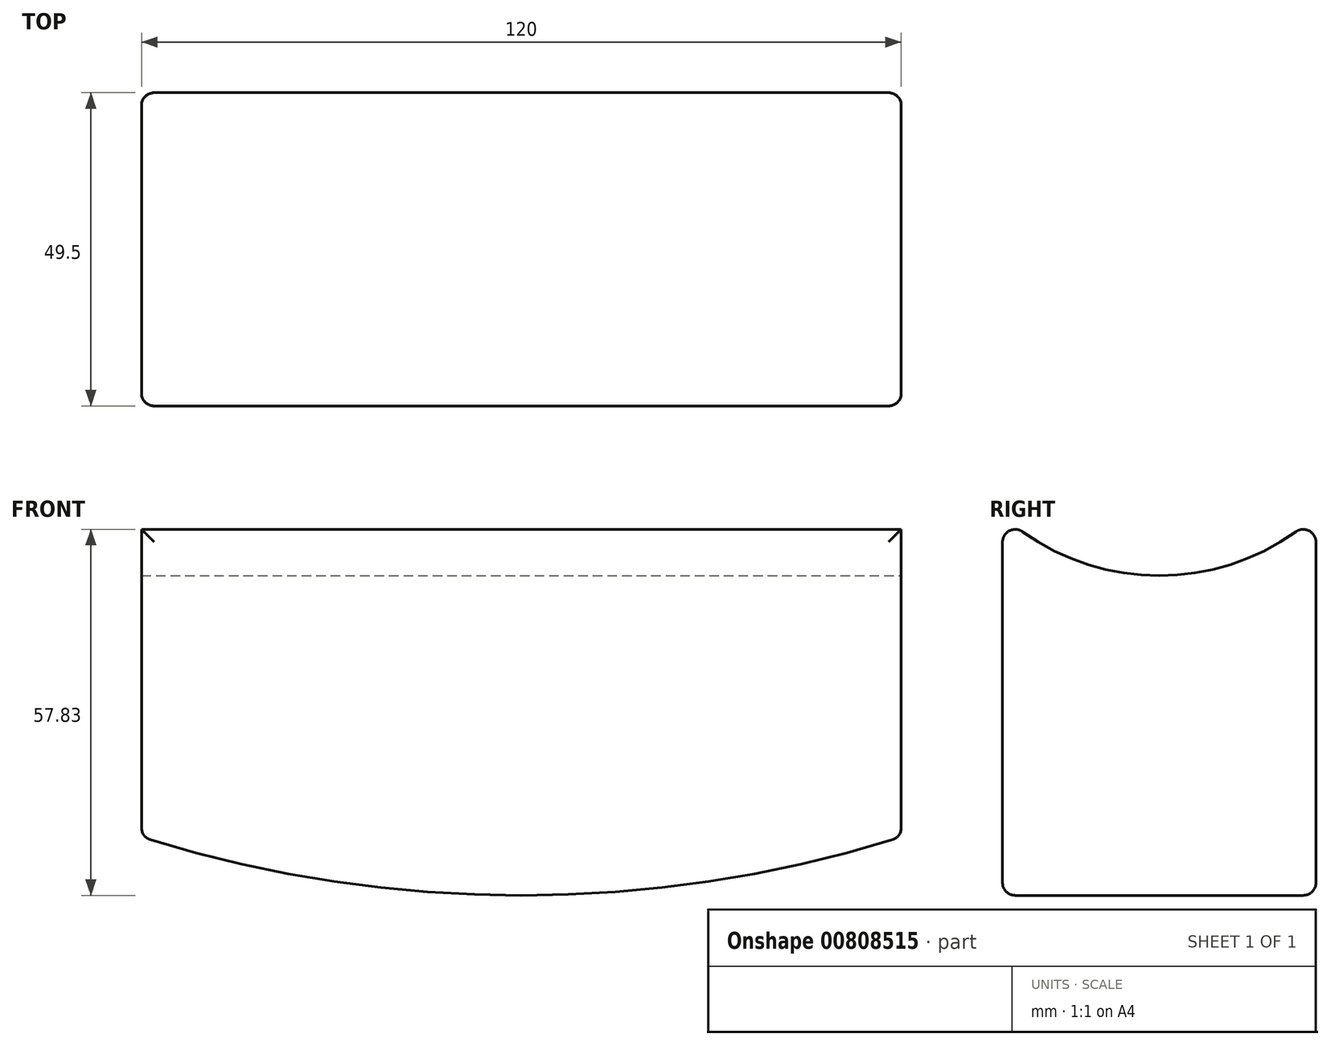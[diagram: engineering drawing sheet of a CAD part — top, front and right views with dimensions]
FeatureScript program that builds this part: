
annotation { "Feature Type Name" : "Feature", "Feature Type Description" : "" }
export const myFeature = defineFeature(function(context is Context, id is Id, definition is map)
    precondition{}
    {
        {
            var Q0;
            Q0=qCreatedBy(makeId("Front.planeOp"),FACE);
            var sketch = newSketch(context, id + "F0", { "sketchPlane" : qUnion([Q0])});
            skLineSegment(sketch, "E0.0.0", {"start": v(73, 24.06) * mm, "end": v(73, 59.5) * mm, "construction": true});
            skLineSegment(sketch, "E0.0.1", {"start": v(73, 59.5) * mm, "end": v(27, 59.5) * mm, "construction": true});
            skLineSegment(sketch, "E0.0.2", {"start": v(27, 59.5) * mm, "end": v(27, 37.72) * mm});
            skLineSegment(sketch, "E0.0.3", {"start": v(27, 37.72) * mm, "end": v(-27, 37.72) * mm});
            skLineSegment(sketch, "E0.0.4", {"start": v(-27, 37.72) * mm, "end": v(-27, 59.5) * mm});
            skLineSegment(sketch, "E0.0.5", {"start": v(-27, 59.5) * mm, "end": v(-73, 59.5) * mm, "construction": true});
            skLineSegment(sketch, "E0.0.6", {"start": v(-73, 59.5) * mm, "end": v(-73, 24.06) * mm, "construction": true});
            skArc(sketch, "E0.0.7", {"start": v(-73, 24.06) * mm, "mid": v(-72.63, 24.02) * mm, "end": v(-72.28, 23.92) * mm});
            skArc(sketch, "E0.0.8", {"start": v(-72.28, 23.92) * mm, "mid": v(0, 10.4) * mm, "end": v(72.28, 23.92) * mm, "construction": true});
            skArc(sketch, "E0.0.9", {"start": v(72.28, 23.92) * mm, "mid": v(72.63, 24.02) * mm, "end": v(73, 24.06) * mm});
            skLineSegment(sketch, "E1", {"start": v(-60, 70.4) * mm, "end": v(60, 70.4) * mm});
            skLineSegment(sketch, "E2", {"start": v(60, 70.4) * mm, "end": v(60, 19.62) * mm});
            skLineSegment(sketch, "E3.MirrorCS", {"start": v(-60, 70.4) * mm, "end": v(-60, 19.62) * mm});
            skArc(sketch, "E4", {"start": v(-60, 19.62) * mm, "mid": v(0, 10.4) * mm, "end": v(60, 19.62) * mm});
            skPoint(sketch, "E5.orphan", {"position": v(60, 81.13) * mm});
            skPoint(sketch, "E6.orphan", {"position": v(60, -3.48) * mm});
            skPoint(sketch, "E7.orphan", {"position": v(-60, -3.48) * mm});
            skPoint(sketch, "E8.orphan", {"position": v(-60, 81.13) * mm});
            skSolve(sketch);
        }
        {
            var Q0;
            Q0 = qSketchRegion(id + "F0", true);
            extrude(context, id + "F1", {"entities" : qUnion([Q0]), "depth" : 49.5 * mm, "offsetDistance" : 25 * mm, "symmetric" : true});
        }
        {
            var Q0;
            Q0=makeQuery(id+"F1.opExtrude","SWEPT_FACE",FACE,{"disambiguationData":[OSD([sQuery(id+"F0.wireOp",EDGE,"E2")])]});
            var sketch = newSketch(context, id + "F2", { "sketchPlane" : qUnion([Q0])});
            skArc(sketch, "E9", {"start": v(-24.75, 70.4) * mm, "mid": v(0, 60.9) * mm, "end": v(24.75, 70.4) * mm});
            skLineSegment(sketch, "E10", {"start": v(-24.75, 70.4) * mm, "end": v(24.75, 70.4) * mm});
            skSolve(sketch);
        }
        {
            var Q0;
            Q0 = qSketchRegion(id + "F2", true);
            extrude(context, id + "F3", {"entities" : qUnion([Q0]), "operationType" : NewBodyOperationType.REMOVE, "oppositeDirection" : true, "depth" : 120 * mm, "offsetDistance" : 25 * mm});
        }
        {
            var Q0;
            {var subQ0=sQuery(id+"F2.wireOp",EDGE,"E10");var subQ1=sQuery(id+"F2.wireOp",EDGE,"E9");var subQ2=sQuery(id+"F0.wireOp",EDGE,"E2");Q0=makeQuery(id+"F3.boolean.opBoolean","MERGE",EDGE,{"derivedFrom":[makeQuery(id+"F1.opExtrude","CAP_EDGE",EDGE,{"disambiguationData":[OSD([sQuery(id+"F0.wireOp",EDGE,"E1")])],"isStart":false}),makeQuery(id+"F3.opExtrude","SWEPT_EDGE",EDGE,{"disambiguationData":[OSD([subQ2,subQ1,subQ0]),TDD([makeQuery(id+"F2.imprint","INTERSECT",VERTEX,{"derivedFrom":[makeQuery(id+"F1.opExtrude","CAP_EDGE",EDGE,{"disambiguationData":[OSD([subQ2])],"isStart":false}),subQ1,subQ0]})])]})]});}
            var Q1;
            {var subQ0=sQuery(id+"F2.wireOp",EDGE,"E10");var subQ1=sQuery(id+"F2.wireOp",EDGE,"E9");var subQ2=sQuery(id+"F0.wireOp",EDGE,"E2");Q1=makeQuery(id+"F3.boolean.opBoolean","MERGE",EDGE,{"derivedFrom":[makeQuery(id+"F1.opExtrude","CAP_EDGE",EDGE,{"disambiguationData":[OSD([sQuery(id+"F0.wireOp",EDGE,"E1")])],"isStart":true}),makeQuery(id+"F3.opExtrude","SWEPT_EDGE",EDGE,{"disambiguationData":[OSD([subQ2,subQ1,subQ0]),TDD([makeQuery(id+"F2.imprint","INTERSECT",VERTEX,{"derivedFrom":[makeQuery(id+"F1.opExtrude","CAP_EDGE",EDGE,{"disambiguationData":[OSD([subQ2])],"isStart":true}),subQ1,subQ0]})])]})]});}
            var Q2;
            Q2=makeQuery(id+"F3.boolean.opBoolean","COPY",EDGE,{"derivedFrom":makeQuery(id+"F3.opExtrude","CAP_EDGE",EDGE,{"disambiguationData":[OSD([sQuery(id+"F2.wireOp",EDGE,"E9")])],"isStart":true})});
            var Q3;
            Q3=makeQuery(id+"F1.opExtrude","CAP_EDGE",EDGE,{"disambiguationData":[OSD([sQuery(id+"F0.wireOp",EDGE,"E2")])],"isStart":false});
            var Q4;
            Q4=makeQuery(id+"F1.opExtrude","CAP_EDGE",EDGE,{"disambiguationData":[OSD([sQuery(id+"F0.wireOp",EDGE,"E2")])],"isStart":true});
            var Q5;
            Q5=makeQuery(id+"F1.opExtrude","SWEPT_EDGE",EDGE,{"disambiguationData":[OSD([sQuery(id+"F0.wireOp",EDGE,"E2"),sQuery(id+"F0.wireOp",EDGE,"E4")])]});
            var Q6;
            Q6=makeQuery(id+"F3.boolean.opBoolean","COPY",EDGE,{"derivedFrom":makeQuery(id+"F3.opExtrude","CAP_EDGE",EDGE,{"disambiguationData":[OSD([sQuery(id+"F2.wireOp",EDGE,"E9")])],"isStart":false})});
            var Q7;
            Q7=makeQuery(id+"F1.opExtrude","CAP_EDGE",EDGE,{"disambiguationData":[OSD([sQuery(id+"F0.wireOp",EDGE,"E3.MirrorCS")])],"isStart":false});
            var Q8;
            Q8=makeQuery(id+"F1.opExtrude","CAP_EDGE",EDGE,{"disambiguationData":[OSD([sQuery(id+"F0.wireOp",EDGE,"E3.MirrorCS")])],"isStart":true});
            var Q9;
            Q9=makeQuery(id+"F1.opExtrude","SWEPT_EDGE",EDGE,{"disambiguationData":[OSD([sQuery(id+"F0.wireOp",EDGE,"E3.MirrorCS"),sQuery(id+"F0.wireOp",EDGE,"E4")])]});
            var Q10;
            Q10=makeQuery(id+"F1.opExtrude","CAP_EDGE",EDGE,{"disambiguationData":[OSD([sQuery(id+"F0.wireOp",EDGE,"E4")])],"isStart":false});
            var Q11;
            Q11=makeQuery(id+"F1.opExtrude","CAP_EDGE",EDGE,{"disambiguationData":[OSD([sQuery(id+"F0.wireOp",EDGE,"E4")])],"isStart":true});
            fillet(context, id + "F4", {"entities" : qUnion([Q0, Q1, Q2, Q3, Q4, Q5, Q6, Q7, Q8, Q9, Q10, Q11]), "radius" : 2 * mm, "tangentPropagation" : true, "allowEdgeOverflow" : false});
        }
    });
